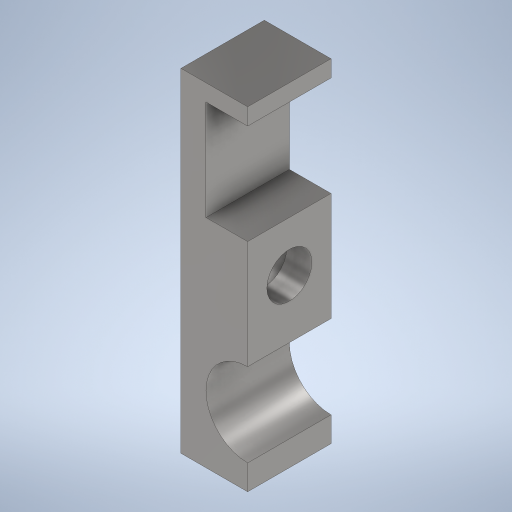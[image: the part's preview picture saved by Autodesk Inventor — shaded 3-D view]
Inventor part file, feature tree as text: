
AUTODESK INVENTOR PART (.ipt)
format: ipt  version: 2023 (Build 270158000, 158)  size: 279,552 bytes
history: native  units: mm
features: extrude x3, sketch x3
ambient origin geometry x8: Origin, YZ Plane, XZ Plane, XY Plane, X Axis, Y Axis, Z Axis, Center Point
bodies: Solid1 (feature_tree)
feature tree (6):
  extrude  "Extrusion1"  Depth=4.0mm
  extrude  "Extrusion2"  Depth=5.0mm
  extrude  "Extrusion3"  Depth=4.0mm
  sketch  "Sketch1"  dims[d0=20.0mm d1=4.0mm]
  sketch  "Sketch3"  dims[d2=5.0mm d3=5.0mm]
  sketch  "Sketch4"  dims[d4=4.0mm d5=4.0mm d6=3.0mm d7=3.0mm d8=5.0mm d9=0.0mm d10=10.0mm d11=2.5mm d12=20.0mm d13=2.7mm d14=20.0mm d15=0.0mm d16=4.9mm d17=2.5mm d18=0.0mm]
